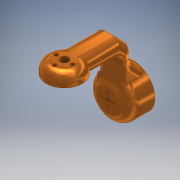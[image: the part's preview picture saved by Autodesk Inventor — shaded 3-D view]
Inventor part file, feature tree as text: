
AUTODESK INVENTOR PART (.ipt)
format: ipt  version: 2017 SP1 (Build 210196100, 196)  size: 473,088 bytes
history: native  units: mm
features: extrude x10, sketch x10, fillet x6, chamfer x4
ambient origin geometry x8: Origin, YZ Plane, XZ Plane, XY Plane, X Axis, Y Axis, Z Axis, Center Point
bodies: Solid1 (feature_tree)
feature tree (30):
  extrude  "Extrusion1"  Depth=35.0mm
  extrude  "Extrusion2"  Depth=8.0mm
  extrude  "Extrusion3"  Depth=3.6mm
  extrude  "Extrusion4"  Depth=3.6mm
  extrude  "Extrusion5"  Depth=42.0mm
  extrude  "Extrusion6"  Depth=13.0mm
  extrude  "Extrusion7"  Depth=2.75mm TaperAngle=0.0deg
  extrude  "Extrusion8"  Depth=14.25mm TaperAngle=0.0deg
  fillet  "Fillet1"  Radius=14.0mm
  extrude  "Extrusion9"  Depth=17.25mm TaperAngle=0.0deg
  chamfer  "Chamfer1"  Distance=2.5mm
  fillet  "Fillet2"  Radius=5.0mm
  chamfer  "Chamfer2"  Distance=5.5mm
  fillet  "Fillet3"  Radius=12.0mm
  fillet  "Fillet4"  Radius=8.0mm
  chamfer  "Chamfer3"  Distance=11.0mm Angle=45.0deg
  chamfer  "Chamfer4"  Distance=8.0mm
  fillet  "Fillet5"  Radius=3.0mm
  fillet  "Fillet6"  Radius=3.0mm
  extrude  "Extrusion10"  Depth=1.5mm TaperAngle=45.0deg
  sketch  "Sketch1"  dims[d0=29.7mm d1=35.0mm]
  sketch  "Sketch2"  dims[d2=4.6mm d3=0.0mm d4=8.0mm]
  sketch  "Sketch4"  dims[d7=3.6mm d8=3.6mm]
  sketch  "Sketch5"  dims[d9=3.6mm d10=3.6mm]
  sketch  "Sketch6"  dims[d11=7.0mm d12=0.0mm d16=42.0mm]
  sketch  "Sketch7"  dims[d17=30.0mm d18=13.0mm]
  sketch  "Sketch8"  dims[d19=24.75mm d20=0.0mm d21=2.75mm d22=0.0mm]
  sketch  "Sketch9"  dims[d23=4.25mm d24=-1.745329mm d25=14.25mm d26=0.0mm d27=14.0mm]
  sketch  "Sketch10"  dims[d28=29.7mm d29=17.25mm d30=0.0mm]
  sketch  "Sketch11"  dims[d33=3.6mm d37=2.5mm d38=6.375mm d39=0.0mm d40=0.0mm d41=5.0mm d42=5.5mm d43=0.0mm d44=12.0mm d45=2.0mm d46=45.0deg d47=8.0mm d48=11.0mm d49=2.0mm d50=45.0deg d51=8.0mm d52=3.0mm d53=3.0mm d54=2.0mm d55=45.0deg d56=1.5mm d57=2.0mm d58=45.0deg d59=8.0mm d60=8.0mm d61=5.5mm d62=4.0mm d63=0.0mm d64=0.0mm]
